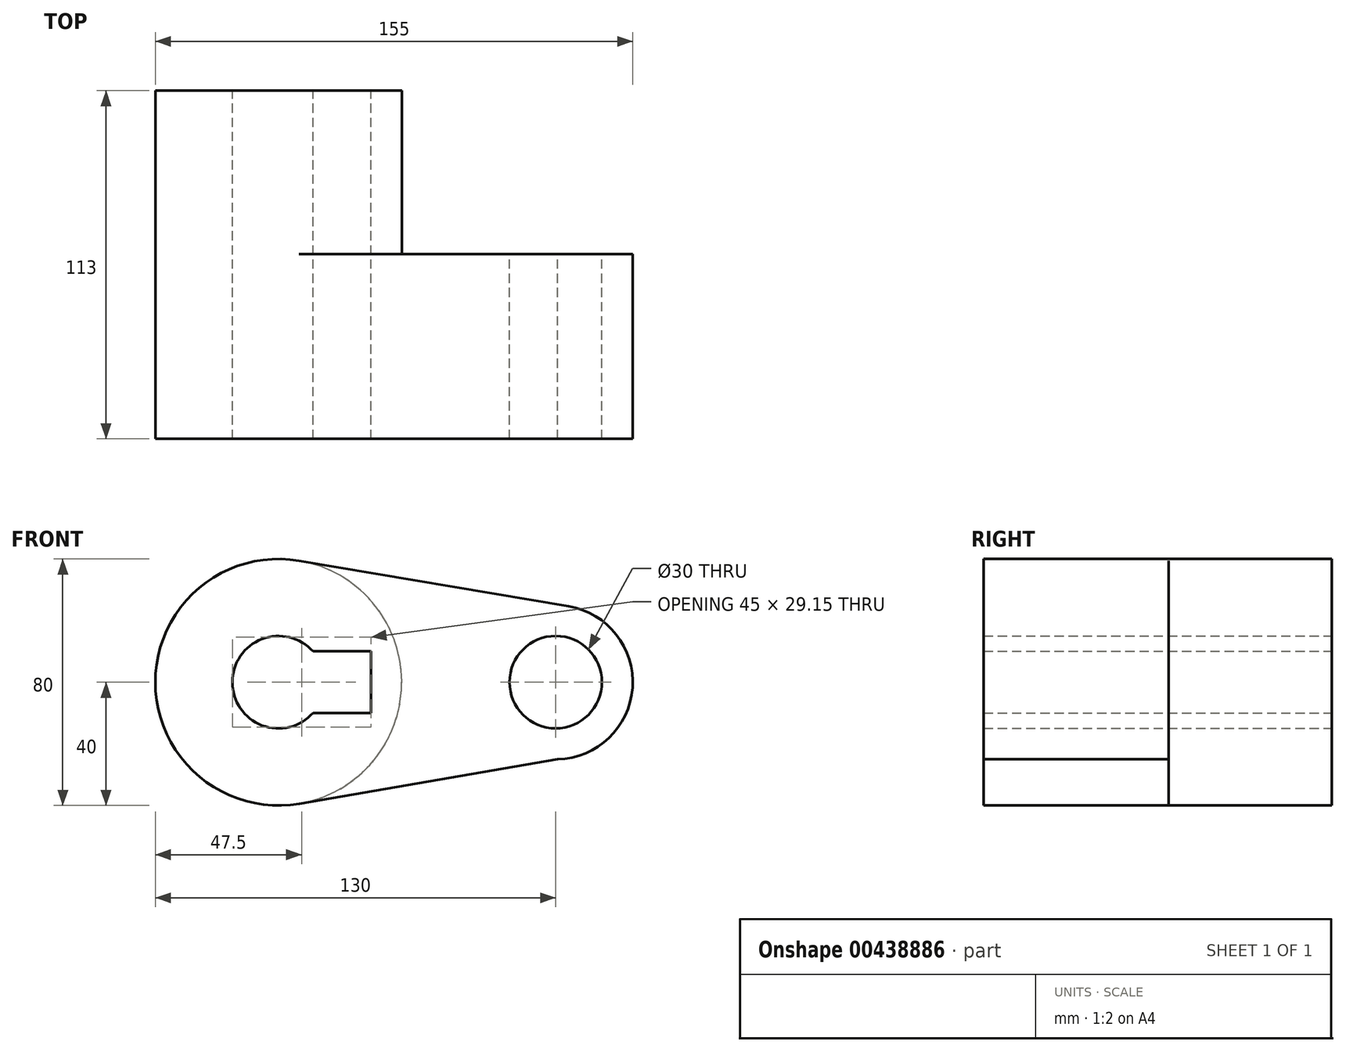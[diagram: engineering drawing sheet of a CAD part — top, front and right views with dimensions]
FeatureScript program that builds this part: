
annotation { "Feature Type Name" : "Feature", "Feature Type Description" : "" }
export const myFeature = defineFeature(function(context is Context, id is Id, definition is map)
    precondition{}
    {
        {
            var Q0;
            Q0=qCreatedBy(makeId("Front.planeOp"),FACE);
            var sketch = newSketch(context, id + "F0", { "sketchPlane" : qUnion([Q0])});
            skCircle(sketch, "E0", {"center": v(0, 0) * mm, "radius": 40 * mm});
            skCircle(sketch, "E1", {"center": v(90, 0) * mm, "radius": 25 * mm});
            skLineSegment(sketch, "E2", {"start": v(6.67, 39.44) * mm, "end": v(94.17, 24.65) * mm});
            skLineSegment(sketch, "E3", {"start": v(6.79, -39.42) * mm, "end": v(90.58, -25) * mm});
            skCircle(sketch, "E4", {"center": v(0, 0) * mm, "radius": 15 * mm});
            skCircle(sketch, "E5", {"center": v(90, 0) * mm, "radius": 15 * mm});
            skLineSegment(sketch, "E6.bottom", {"start": v(30, 10) * mm, "end": v(-30, 10) * mm});
            skLineSegment(sketch, "E6.top", {"start": v(30, -10) * mm, "end": v(-30, -10) * mm});
            skLineSegment(sketch, "E6.left", {"start": v(30, 10) * mm, "end": v(30, -10) * mm});
            skLineSegment(sketch, "E6.right", {"start": v(-30, 10) * mm, "end": v(-30, -10) * mm});
            skSolve(sketch);
        }
        {
            var Q0;
            {var subQ7=sQuery(id+"F0.wireOp",EDGE,"E6.left");Q0=makeQuery(id+"F0.imprint","IMPRINT",FACE,{"disambiguationData":[TD([[makeQuery(id+"F0.imprint","IMPRINT",EDGE,{"derivedFrom":subQ7}),1.0]])]});}
            var Q1;
            {var subQ5=sQuery(id+"F0.wireOp",EDGE,"E6.right");Q1=makeQuery(id+"F0.imprint","IMPRINT",FACE,{"disambiguationData":[TD([[makeQuery(id+"F0.imprint","IMPRINT",EDGE,{"derivedFrom":subQ5}),1.0]])]});}
            var Q2;
            {var subQ0=sQuery(id+"F0.wireOp",EDGE,"E2");Q2=makeQuery(id+"F0.imprint","IMPRINT",FACE,{"disambiguationData":[TD([[makeQuery(id+"F0.imprint","IMPRINT",EDGE,{"derivedFrom":subQ0}),-1.0]])]});}
            var Q3;
            Q3=makeQuery(id+"F0.imprint","IMPRINT",FACE,{"disambiguationData":[TD([[makeQuery(id+"F0.imprint","IMPRINT",EDGE,{"derivedFrom":sQuery(id+"F0.wireOp",EDGE,"E5")}),-1.0]])]});
            extrude(context, id + "F1", {"entities" : qUnion([Q0, Q1, Q2, Q3]), "depth" : 60 * mm});
        }
        {
            var Q0;
            {var subQ5=sQuery(id+"F0.wireOp",EDGE,"E6.right");Q0=makeQuery(id+"F0.imprint","IMPRINT",FACE,{"disambiguationData":[TD([[makeQuery(id+"F0.imprint","IMPRINT",EDGE,{"derivedFrom":subQ5}),1.0]])]});}
            var Q1;
            {var subQ7=sQuery(id+"F0.wireOp",EDGE,"E6.left");Q1=makeQuery(id+"F0.imprint","IMPRINT",FACE,{"disambiguationData":[TD([[makeQuery(id+"F0.imprint","IMPRINT",EDGE,{"derivedFrom":subQ7}),1.0]])]});}
            extrude(context, id + "F2", {"entities" : qUnion([Q0, Q1]), "operationType" : NewBodyOperationType.ADD, "oppositeDirection" : true, "depth" : 53 * mm});
        }
    });
